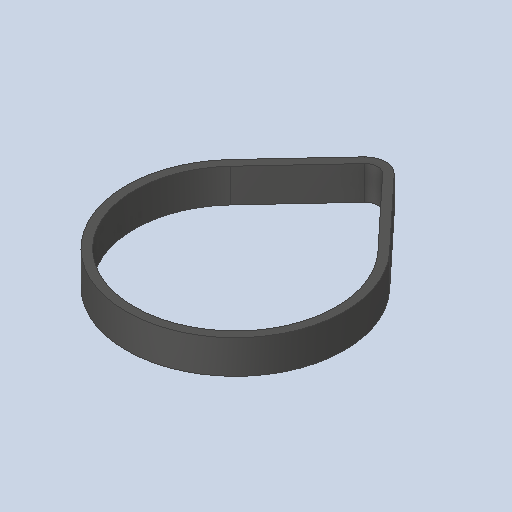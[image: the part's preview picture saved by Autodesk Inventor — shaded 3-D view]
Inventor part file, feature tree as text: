
AUTODESK INVENTOR PART (.ipt)
format: ipt  version: 2023 (Build 270158000, 158)  size: 94,720 bytes
history: native  units: in
note: dims shown in document units (in); Inventor stores cm internally (conversion verified against a paired STEP export)
features: extrude x1
ambient origin geometry x8: Origin, YZ Plane, XZ Plane, XY Plane, X Axis, Y Axis, Z Axis, Center Point
bodies: Solid1 (feature_tree)
feature tree (1):
  extrude  "Extrude-Thin1"  [1 undecoded]
note: 1 required parameter value undecoded (feature->parameter linkage not recoverable at this tier; creation-order binding heuristic only, values carry confidence <= 0.55)
